# Revit family: Hager-Volta-IP30-Hollow_wall-syst-FR-fr
name_source: partatom
category: Electrical Equipment
units: mm (PartAtom-declared; Revit-internal decimal feet)

## family parameters
Cut with Voids When Loaded = No
Host = Face
Panel Configuration = Two Columns, Circuits Across
Part Type = Panelboard
Room Calculation Point = No
Round Connector Dimension = Use Diameter
Shared = No

## types (4) — shared parameters
EF000003 - mode de pose = EV000128 - mur creux
EF000007 - couleur = EV000202 - blanc
EF000008 - largeur = 348 mm  [stored 1.14173 ft]
EF000049 - profondeur = 98 mm  [stored 0.321522 ft]
EF000116 - numéro RAL = 9010
EF000118 - avec cadre/support de montage = No
EF000218 - profondeur d'encastrement = 89 mm  [stored 0.291995 ft]
EF000339 - type de capot = EV004216 - porte
EF000846 - largeur d'encastrement = 314 mm  [stored 1.03018 ft]
EF001062 - finition CEM = No
EF001088 - possibilité de montage en saillie = Yes
EF001134 - rail DIN = No
EF001596 - matériau du boîtier/corps = EV000139 - plastique
EF002950 - largeur en nombre de modules = 12
EF004462 - type de fermeture = EV000154 - autre
EF005474 - indice de protection (IP) = EV006410 - IP30
EF006244 - couvercle/porte transparent(e) = No
EF006306 - avec serrure = No
EF015776 - borne de mise à la terre = Yes
EF015777 - borne à conducteur neutre = No
EF015941 - porte pour transmission du signal = No
HG000001 - nombre de colonnes = 1
HG000002 - avec porte = Yes
HG000003 - Gamme = Volta
HG000005 - Epaisseur = 3 mm  [stored 0.00984252 ft]
HG000006 - Encastré = Yes
HG000009 - Porte à double battant = No
HG000010 - Portes asymétriques = No
HG000011 - Rangées du bas vides = No
HG000017 - Distance entre pôles = 18 mm  [stored 0.0590551 ft]
Manufacturer = Hager
Type Comments = Volta
zero-valued in all types: Default Elevation, EF001131 - profondeur intérieure, HG000007 - Nombre de colonnes vides, HG000008 - Nombre de rangées vides

## per-type parameters (varying)
| type | EF000040 - hauteur | EF000266 - nombre de rangées | EF000332 - hauteur d'encastrement | HG000004 - Référence fabricant | Model |
| Encastré IP30 L348 H356.5 P98 12 Modules - VU12ND | 356 mm | 1 | 321 mm | VU12ND | VU12ND |
| Encastré IP30 L348 H505.5 P98 12 Modules - VU24ND | 506 mm | 2 | 470 mm | VU24ND | VU24ND |
| Encastré IP30 L348 H630.5 P98 12 Modules - VU36ND | 630 mm | 3 | 595 mm | VU36ND | VU36ND |
| Encastré IP30 L348 H755.5 P98 12 Modules - VU48ND | 756 mm  [stored 2.48031 ft] | 4 | 720 mm  [stored 2.3622 ft] | VU48ND | VU48ND |

note: [stored X ft] marks values corroborated as IEEE doubles in the binary element streams (Revit-internal decimal feet)

## geometry (parser evidence)
native form markers: Sweep x17
no freeform markers — native parametric forms only
